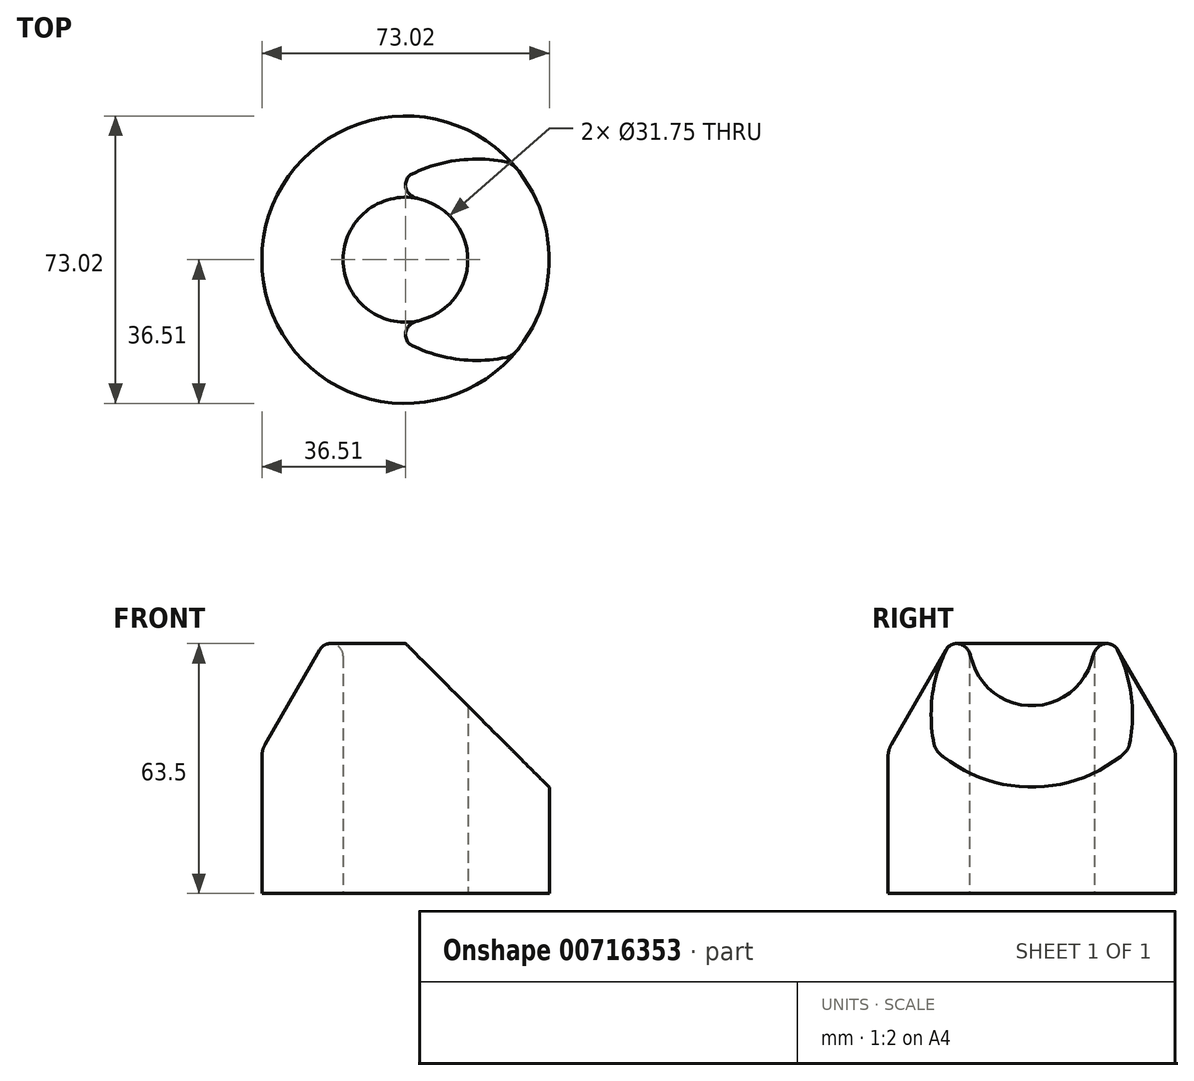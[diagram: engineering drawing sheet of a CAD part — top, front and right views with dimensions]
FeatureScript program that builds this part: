
annotation { "Feature Type Name" : "Feature", "Feature Type Description" : "" }
export const myFeature = defineFeature(function(context is Context, id is Id, definition is map)
    precondition{}
    {
        {
            var Q0;
            Q0=qCreatedBy(makeId("Front.planeOp"),FACE);
            var sketch = newSketch(context, id + "F0", { "sketchPlane" : qUnion([Q0])});
            skLineSegment(sketch, "E0.bottom", {"start": v(-15.88, 0) * mm, "end": v(-36.51, 0) * mm});
            skLineSegment(sketch, "E0.top", {"start": v(-15.88, 63.5) * mm, "end": v(-36.51, 63.5) * mm});
            skLineSegment(sketch, "E0.left", {"start": v(-15.88, 0) * mm, "end": v(-15.88, 63.5) * mm});
            skLineSegment(sketch, "E0.right", {"start": v(-36.51, 0) * mm, "end": v(-36.51, 63.5) * mm});
            skLineSegment(sketch, "E1", {"start": v(0, 0) * mm, "end": v(0, 53.86) * mm, "construction": true});
            skCircle(sketch, "E2", {"center": v(-19.05, 60.33) * mm, "radius": 3.18 * mm});
            skLineSegment(sketch, "E3", {"start": v(-21.8, 61.91) * mm, "end": v(-36.51, 36.43) * mm});
            skSolve(sketch);
        }
        {
            var Q0;
            {var subQ0=sQuery(id+"F0.wireOp",EDGE,"E2");var subQ1=makeQuery(id+"F0.imprint","INTERSECT",VERTEX,{"derivedFrom":[sQuery(id+"F0.wireOp",EDGE,"E0.top"),subQ0]});Q0=makeQuery(id+"F0.imprint","IMPRINT",FACE,{"disambiguationData":[TD([[makeQuery(id+"F0.imprint","IMPRINT",EDGE,{"disambiguationData":[TD([[subQ1,1.0]])],"derivedFrom":subQ0}),1.0]])]});}
            var Q1;
            {var subQ4=sQuery(id+"F0.wireOp",EDGE,"E0.bottom");Q1=makeQuery(id+"F0.imprint","IMPRINT",FACE,{"disambiguationData":[TD([[makeQuery(id+"F0.imprint","IMPRINT",EDGE,{"derivedFrom":subQ4}),-1.0]])]});}
            var Q2;
            Q2=sQuery(id+"F0.wireOp",EDGE,"E1");
            revolve(context, id + "F1", {"surfaceOperationType" : NewSurfaceOperationType.NEW, "entities" : qUnion([Q0, Q1]), "axis" : qUnion([Q2]), "revolveType" : RevolveType.FULL});
        }
        {
            var Q0;
            Q0=makeQuery(id+"F1.opRevolve","SWEPT_EDGE",EDGE,{"disambiguationData":[OSD([sQuery(id+"F0.wireOp",EDGE,"E0.right"),sQuery(id+"F0.wireOp",EDGE,"E3")])]});
            fillet(context, id + "F2", {"entities" : qUnion([Q0]), "radius" : 6.35 * mm, "tangentPropagation" : true, "allowEdgeOverflow" : false});
        }
        {
            var Q0;
            Q0=qCreatedBy(makeId("Front.planeOp"),FACE);
            var sketch = newSketch(context, id + "F3", { "sketchPlane" : qUnion([Q0])});
            skLineSegment(sketch, "E4", {"start": v(0, 0) * mm, "end": v(0, 113.27) * mm, "construction": true});
            skLineSegment(sketch, "E5", {"start": v(0, 63.5) * mm, "end": v(50.8, 12.7) * mm});
            skLineSegment(sketch, "E6", {"start": v(0, 63.5) * mm, "end": v(0, 88.9) * mm});
            skLineSegment(sketch, "E7", {"start": v(0, 88.9) * mm, "end": v(50.8, 88.9) * mm});
            skLineSegment(sketch, "E8", {"start": v(50.8, 88.9) * mm, "end": v(50.8, 12.7) * mm});
            skSolve(sketch);
        }
        {
            var Q0;
            Q0 = qSketchRegion(id + "F3", true);
            extrude(context, id + "F4", {"entities" : qUnion([Q0]), "operationType" : NewBodyOperationType.REMOVE, "endBound" : BoundingType.SYMMETRIC, "oppositeDirection" : true, "depth" : 254 * mm, "offsetDistance" : 25.4 * mm});
        }
    });
